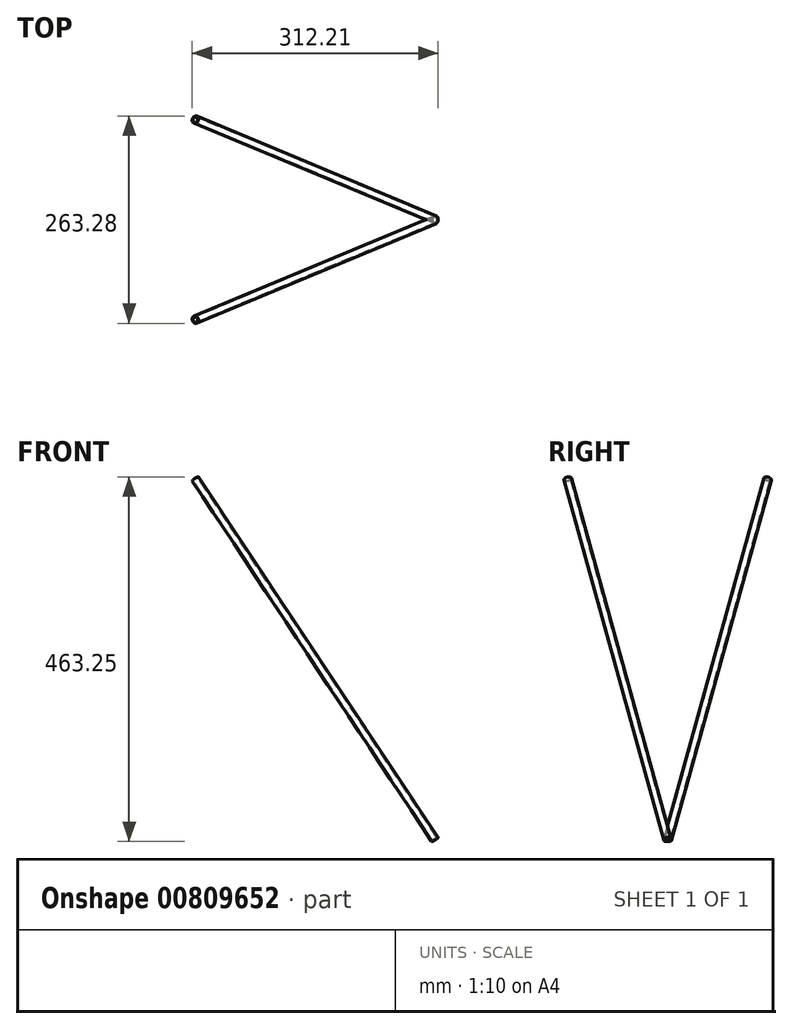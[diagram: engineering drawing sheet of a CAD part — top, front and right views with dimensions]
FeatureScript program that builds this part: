
annotation { "Feature Type Name" : "Feature", "Feature Type Description" : "" }
export const myFeature = defineFeature(function(context is Context, id is Id, definition is map)
    precondition{}
    {
        {
            var Q0;
            Q0=qCreatedBy(makeId("Right.planeOp"),FACE);
            var sketch = newSketch(context, id + "F0", { "sketchPlane" : qUnion([Q0])});
            skPoint(sketch, "E0", {"position": v(-127, 0) * mm});
            skSolve(sketch);
        }
        {
            var Q0;
            Q0=qCreatedBy(makeId("Right.planeOp"),FACE);
            cPlane(context, id + "F1", {"entities" : qUnion([Q0]), "cplaneType" : CPlaneType.OFFSET, "offset" : 25.4 * mm, "width" : 152.4 * mm, "height" : 152.4 * mm});
        }
        {
            var Q0;
            Q0=qCreatedBy(id+"F1.planeOp",FACE);
            var sketch = newSketch(context, id + "F2", { "sketchPlane" : qUnion([Q0])});
            skPoint(sketch, "E1", {"position": v(-187.96, 0) * mm});
            skPoint(sketch, "E2", {"position": v(-187.96, 50.8) * mm});
            skSolve(sketch);
        }
        {
            var Q0;
            Q0=sQuery(id+"F2.wireOp",VERTEX,"E2");
            var Q1;
            Q1=sQuery(id+"F0.wireOp",VERTEX,"E0");
            var Q2;
            Q2=sQuery(id+"F2.wireOp",VERTEX,"E1");
            cPlane(context, id + "F3", {"entities" : qUnion([Q0, Q1, Q2]), "cplaneType" : CPlaneType.THREE_POINT, "offset" : 25.4 * mm, "width" : 152.4 * mm, "height" : 152.4 * mm});
        }
        {
            var Q0;
            Q0=qCreatedBy(id+"F3.planeOp",FACE);
            cPlane(context, id + "F4", {"entities" : qUnion([Q0]), "cplaneType" : CPlaneType.OFFSET, "offset" : 25.4 * mm, "width" : 152.4 * mm, "height" : 152.4 * mm});
        }
        {
            var Q0;
            Q0=qCreatedBy(id+"F4.planeOp",FACE);
            var sketch = newSketch(context, id + "F5", { "sketchPlane" : qUnion([Q0])});
            skPoint(sketch, "E3", {"position": v(-137.13, 18.29) * mm});
            skSolve(sketch);
        }
        {
            var Q0;
            Q0=sQuery(id+"F5.wireOp",VERTEX,"E3");
            var Q1;
            Q1=sQuery(id+"F0.wireOp",VERTEX,"E0");
            var Q2;
            Q2=sQuery(id+"F2.wireOp",VERTEX,"E1");
            cPlane(context, id + "F6", {"entities" : qUnion([Q0, Q1, Q2]), "cplaneType" : CPlaneType.THREE_POINT, "offset" : 25.4 * mm, "width" : 152.4 * mm, "height" : 152.4 * mm});
        }
        {
            var Q0;
            Q0=qCreatedBy(id+"F6.planeOp",FACE);
            var sketch = newSketch(context, id + "F7", { "sketchPlane" : qUnion([Q0])});
            skCircle(sketch, "E4", {"center": v(18.28, 122.4) * mm, "radius": 4.76 * mm});
            skCircle(sketch, "E5", {"center": v(18.28, 122.4) * mm, "radius": 3.52 * mm});
            skSolve(sketch);
        }
        {
            var Q0;
            Q0=makeQuery(id+"F7.imprint","IMPRINT",FACE,{"disambiguationData":[TD([[makeQuery(id+"F7.imprint","IMPRINT",EDGE,{"derivedFrom":sQuery(id+"F7.wireOp",EDGE,"E4")}),1.0]])]});
            extrude(context, id + "F8", {"entities" : qUnion([Q0]), "depth" : 563.98 * mm, "offsetDistance" : 25.4 * mm});
        }
        {
            var Q0;
            Q0=makeQuery(id+"F8.opExtrude","SWEPT_BODY",BODY,{"disambiguationData":[OSD([sQuery(id+"F7.wireOp",EDGE,"E4"),sQuery(id+"F7.wireOp",EDGE,"E5")])]});
            var Q1;
            Q1=qCreatedBy(makeId("Front.planeOp"),FACE);
            mirror(context, id + "F9", {"entities" : qUnion([Q0]), "mirrorPlane" : qUnion([Q1])});
        }
    });
